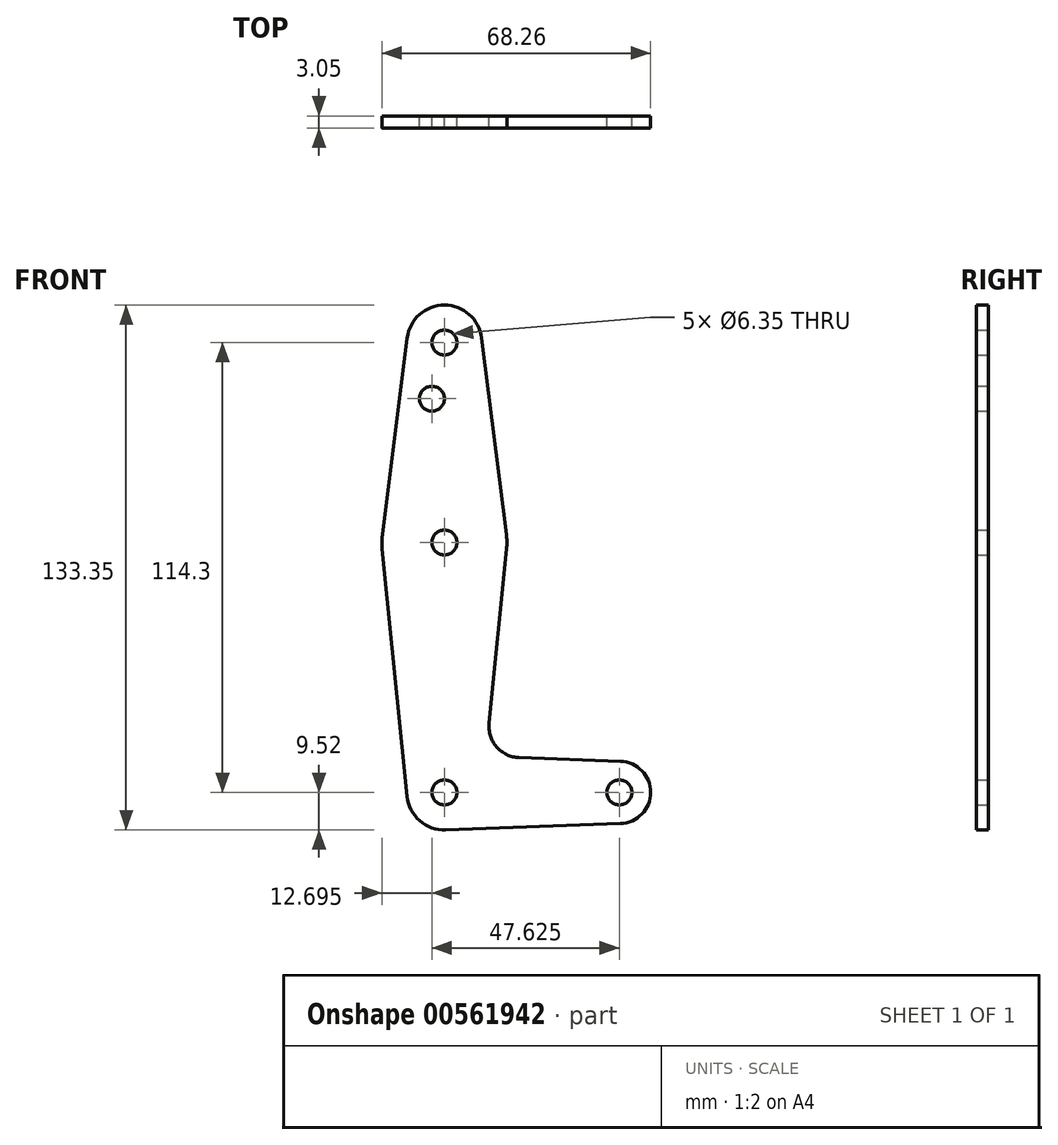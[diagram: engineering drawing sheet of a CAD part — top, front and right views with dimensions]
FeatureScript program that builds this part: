
annotation { "Feature Type Name" : "Feature", "Feature Type Description" : "" }
export const myFeature = defineFeature(function(context is Context, id is Id, definition is map)
    precondition{}
    {
        {
            var Q0;
            Q0=qCreatedBy(makeId("Front.planeOp"),FACE);
            var sketch = newSketch(context, id + "F0", { "sketchPlane" : qUnion([Q0])});
            skLineSegment(sketch, "E0", {"start": v(0, 0) * mm, "end": v(44.45, 0) * mm, "construction": true});
            skLineSegment(sketch, "E1", {"start": v(0, 0) * mm, "end": v(0, 114.3) * mm, "construction": true});
            skCircle(sketch, "E2", {"center": v(0, 114.3) * mm, "radius": 9.53 * mm});
            skCircle(sketch, "E3", {"center": v(0, 63.5) * mm, "radius": 15.88 * mm});
            skCircle(sketch, "E4", {"center": v(0, 0) * mm, "radius": 9.53 * mm});
            skCircle(sketch, "E5", {"center": v(44.45, 0) * mm, "radius": 7.94 * mm});
            skLineSegment(sketch, "E6", {"start": v(9.45, 115.5) * mm, "end": v(15.75, 65.48) * mm});
            skLineSegment(sketch, "E7", {"start": v(-9.45, 115.5) * mm, "end": v(-15.75, 65.48) * mm});
            skCircle(sketch, "E8", {"center": v(0, 114.3) * mm, "radius": 3.18 * mm});
            skCircle(sketch, "E9", {"center": v(0, 63.5) * mm, "radius": 3.18 * mm});
            skCircle(sketch, "E10", {"center": v(-3.18, 100.03) * mm, "radius": 3.18 * mm});
            skCircle(sketch, "E11", {"center": v(44.45, 0) * mm, "radius": 3.18 * mm});
            skCircle(sketch, "E12", {"center": v(0, 0) * mm, "radius": 3.18 * mm});
            skPoint(sketch, "E13", {"position": v(22.23, 0) * mm});
            skLineSegment(sketch, "E14", {"start": v(-15.8, 61.91) * mm, "end": v(-9.48, -0.95) * mm});
            skLineSegment(sketch, "E15", {"start": v(15.8, 61.91) * mm, "end": v(11.34, 17.6) * mm});
            skLineSegment(sketch, "E16", {"start": v(18.97, 8.85) * mm, "end": v(44.73, 7.93) * mm});
            skLineSegment(sketch, "E17", {"start": v(0.34, -9.52) * mm, "end": v(44.73, -7.93) * mm});
            skArc(sketch, "E18.filletArc", {"start": v(11.34, 17.6) * mm, "mid": v(13.26, 11.57) * mm, "end": v(18.97, 8.85) * mm});
            skSolve(sketch);
        }
        {
            var Q0;
            Q0 = qSketchRegion(id + "F0", true);
            extrude(context, id + "F1", {"entities" : qUnion([Q0]), "depth" : 3.05 * mm, "offsetDistance" : 25.4 * mm});
        }
    });
